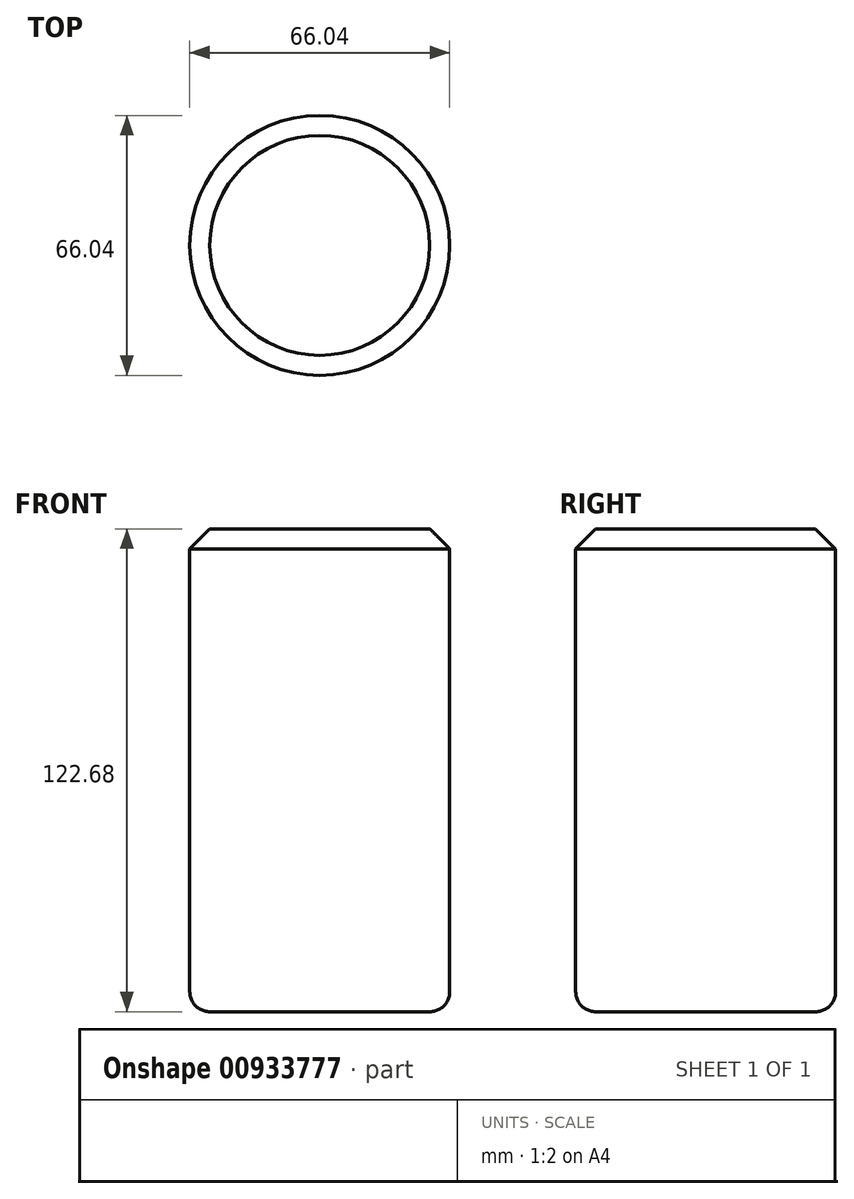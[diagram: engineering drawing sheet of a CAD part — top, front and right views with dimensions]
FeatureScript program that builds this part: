
annotation { "Feature Type Name" : "Feature", "Feature Type Description" : "" }
export const myFeature = defineFeature(function(context is Context, id is Id, definition is map)
    precondition{}
    {
        {
            var Q0;
            Q0=qCreatedBy(makeId("Top.planeOp"),FACE);
            var sketch = newSketch(context, id + "F0", { "sketchPlane" : qUnion([Q0])});
            skCircle(sketch, "E0", {"center": v(0, 0) * mm, "radius": 33.02 * mm});
            skSolve(sketch);
        }
        {
            var Q0;
            Q0=makeQuery(id+"F0.imprint","IMPRINT",FACE,{"disambiguationData":[TD([[makeQuery(id+"F0.imprint","IMPRINT",EDGE,{"derivedFrom":sQuery(id+"F0.wireOp",EDGE,"E0")}),1.0]])]});
            extrude(context, id + "F1", {"entities" : qUnion([Q0]), "depth" : 122.68 * mm, "offsetDistance" : 25.4 * mm});
        }
        {
            var Q0;
            Q0=makeQuery(id+"F1.opExtrude","CAP_EDGE",EDGE,{"disambiguationData":[OSD([sQuery(id+"F0.wireOp",EDGE,"E0")])],"isStart":true});
            fillet(context, id + "F2", {"entities" : qUnion([Q0]), "radius" : 5.08 * mm, "tangentPropagation" : true, "allowEdgeOverflow" : false});
        }
        {
            var Q0;
            Q0=makeQuery(id+"F1.opExtrude","CAP_EDGE",EDGE,{"disambiguationData":[OSD([sQuery(id+"F0.wireOp",EDGE,"E0")])],"isStart":false});
            chamfer(context, id + "F3", {"entities" : qUnion([Q0]), "width" : 5.08 * mm, "tangentPropagation" : true});
        }
    });
